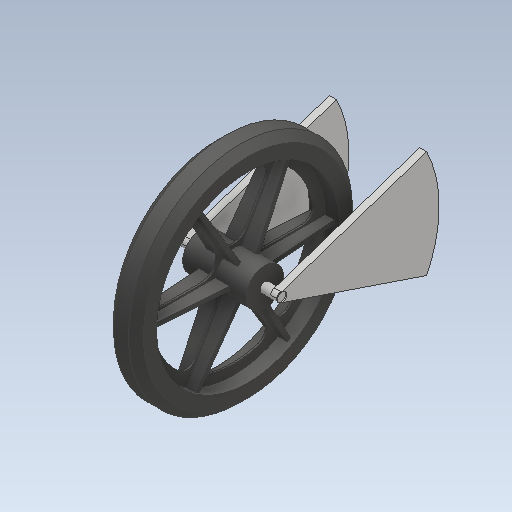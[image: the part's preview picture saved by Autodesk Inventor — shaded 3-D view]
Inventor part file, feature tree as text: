
AUTODESK INVENTOR PART (.ipt)
format: ipt  version: 2020 (Build 240168000, 168)  size: 361,472 bytes
history: native  units: mm
features: other x3, extrude x3, sketch x3, thicken_offset x2, plane x1, mirror x1
ambient origin geometry x8: Origin, YZ Plane, XZ Plane, XY Plane, X Axis, Y Axis, Z Axis, Center Point
bodies: Solid1 (feature_tree)
feature tree (13):
  other  "wheel.ipt"
  extrude  "Extrusion1"  TaperAngle=0.0deg  [1 undecoded]
  extrude  "Extrusion2"  TaperAngle=0.0deg  [1 undecoded]
  extrude  "Extrusion3"  Depth=30.0mm
  plane  "Work Plane1"
  mirror  "Mirror1"
  thicken_offset  "Thicken1"
  thicken_offset  "Thicken2"
  other  "Solid19::wheel.ipt"
  other  "TaggingFeature1"
  sketch  "Sketch1"  dims[d0=5.0mm d2=0.0mm]
  sketch  "Sketch2"  dims[d4=0.0mm d6=0.0mm]
  sketch  "Sketch3"  dims[d9=30.0mm d11=30.0mm]
note: 2 required parameter values undecoded (feature->parameter linkage not recoverable at this tier; creation-order binding heuristic only, values carry confidence <= 0.55)
